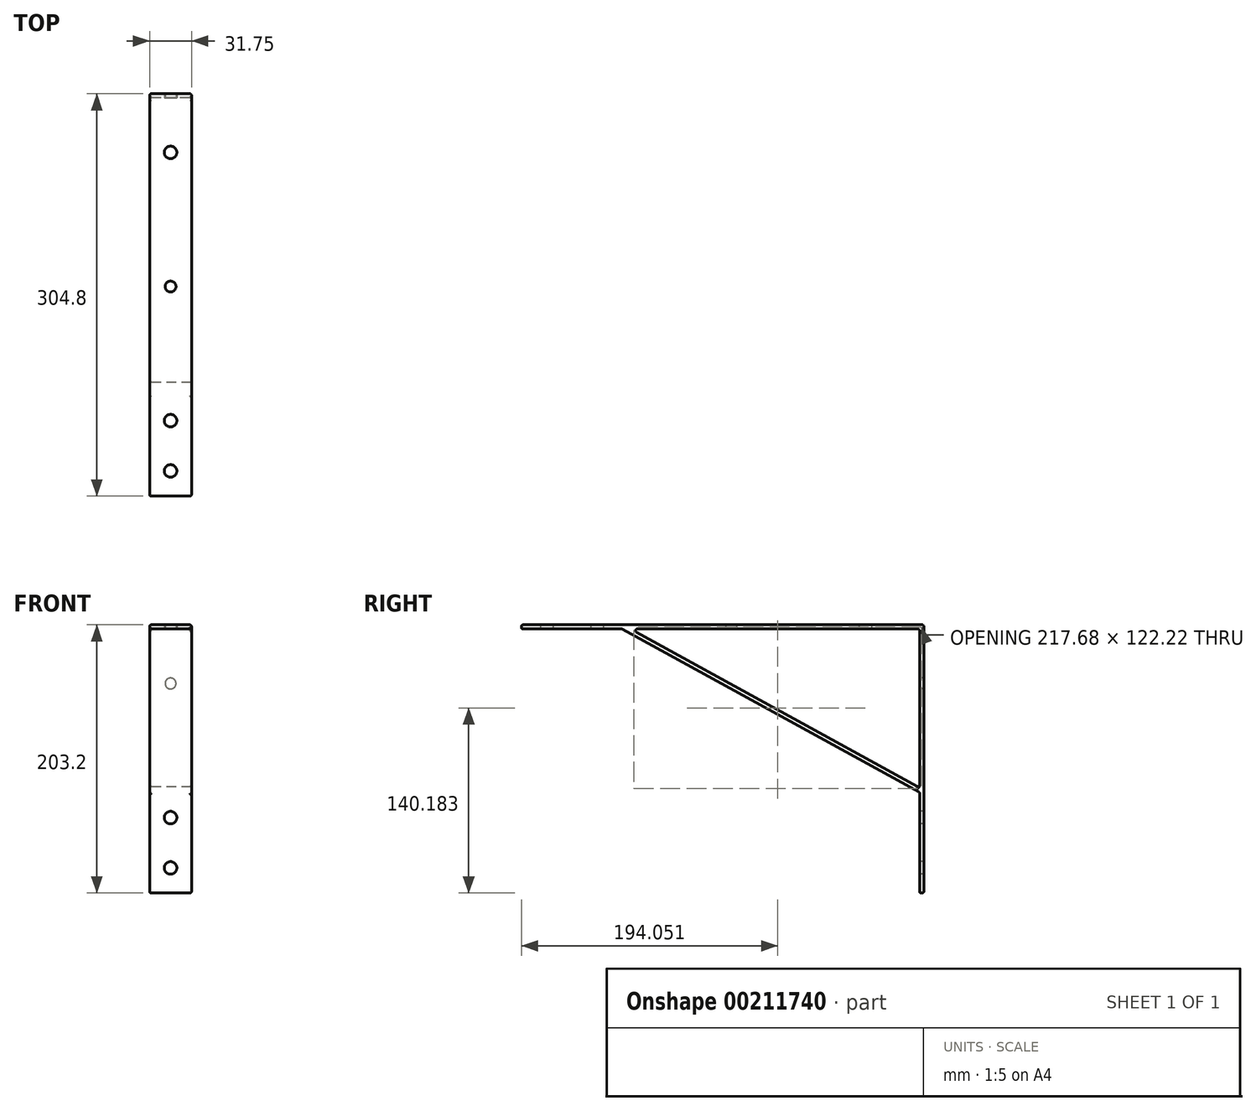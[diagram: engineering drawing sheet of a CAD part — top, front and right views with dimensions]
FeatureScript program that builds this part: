
annotation { "Feature Type Name" : "Feature", "Feature Type Description" : "" }
export const myFeature = defineFeature(function(context is Context, id is Id, definition is map)
    precondition{}
    {
        {
            var Q0;
            Q0=qCreatedBy(makeId("Right.planeOp"),FACE);
            var sketch = newSketch(context, id + "F0", { "sketchPlane" : qUnion([Q0])});
            skLineSegment(sketch, "E0", {"start": v(-304.8, 203.2) * mm, "end": v(0, 203.2) * mm});
            skLineSegment(sketch, "E1", {"start": v(0, 203.2) * mm, "end": v(0, 0) * mm});
            skLineSegment(sketch, "E2", {"start": v(0, 0) * mm, "end": v(-3.17, 0) * mm});
            skLineSegment(sketch, "E3", {"start": v(-3.17, 0) * mm, "end": v(-3.18, 76.2) * mm});
            skLineSegment(sketch, "E4", {"start": v(-3.18, 200.03) * mm, "end": v(-222, 200.02) * mm});
            skLineSegment(sketch, "E5", {"start": v(-304.8, 200.02) * mm, "end": v(-304.8, 203.2) * mm});
            skLineSegment(sketch, "E6", {"start": v(-222, 200.03) * mm, "end": v(-3.18, 79.82) * mm});
            skLineSegment(sketch, "E7", {"start": v(-3.18, 76.2) * mm, "end": v(-228.6, 200.02) * mm});
            skLineSegment(sketch, "E8.trimOffspring", {"start": v(-228.6, 200.02) * mm, "end": v(-304.8, 200.02) * mm});
            skLineSegment(sketch, "E9.trimOffspring", {"start": v(-3.18, 79.82) * mm, "end": v(-3.18, 200.03) * mm});
            skSolve(sketch);
        }
        {
            var Q0;
            Q0 = qSketchRegion(id + "F0", true);
            extrude(context, id + "F1", {"entities" : qUnion([Q0]), "depth" : 31.75 * mm});
        }
        {
            var Q0;
            Q0=makeQuery(id+"F1.opExtrude","CAP_EDGE",EDGE,{"disambiguationData":[OSD([sQuery(id+"F0.wireOp",EDGE,"E6")])],"isStart":false});
            var Q1;
            Q1=makeQuery(id+"F1.opExtrude","CAP_EDGE",EDGE,{"disambiguationData":[OSD([sQuery(id+"F0.wireOp",EDGE,"E7")])],"isStart":false});
            var Q2;
            Q2=makeQuery(id+"F1.opExtrude","CAP_EDGE",EDGE,{"disambiguationData":[OSD([sQuery(id+"F0.wireOp",EDGE,"E7")])],"isStart":true});
            var Q3;
            Q3=makeQuery(id+"F1.opExtrude","CAP_EDGE",EDGE,{"disambiguationData":[OSD([sQuery(id+"F0.wireOp",EDGE,"E6")])],"isStart":true});
            var Q4;
            Q4=makeQuery(id+"F1.opExtrude","SWEPT_EDGE",EDGE,{"disambiguationData":[OSD([sQuery(id+"F0.wireOp",EDGE,"E3"),sQuery(id+"F0.wireOp",EDGE,"E7")])]});
            var Q5;
            Q5=makeQuery(id+"F1.opExtrude","SWEPT_EDGE",EDGE,{"disambiguationData":[OSD([sQuery(id+"F0.wireOp",EDGE,"E7"),sQuery(id+"F0.wireOp",EDGE,"E8.trimOffspring")])]});
            fillet(context, id + "F2", {"entities" : qUnion([Q0, Q1, Q2, Q3, Q4, Q5]), "radius" : 1.27 * mm, "tangentPropagation" : true, "allowEdgeOverflow" : false});
        }
        {
            var Q0;
            Q0=makeQuery(id+"F1.opExtrude","SWEPT_EDGE",EDGE,{"disambiguationData":[OSD([sQuery(id+"F0.wireOp",EDGE,"E6"),sQuery(id+"F0.wireOp",EDGE,"E9.trimOffspring")])]});
            var Q1;
            Q1=makeQuery(id+"F1.opExtrude","SWEPT_EDGE",EDGE,{"disambiguationData":[OSD([sQuery(id+"F0.wireOp",EDGE,"E4"),sQuery(id+"F0.wireOp",EDGE,"E6")])]});
            var Q2;
            Q2=makeQuery(id+"F1.opExtrude","SWEPT_EDGE",EDGE,{"disambiguationData":[OSD([sQuery(id+"F0.wireOp",EDGE,"E4"),sQuery(id+"F0.wireOp",EDGE,"E9.trimOffspring")])]});
            var Q3;
            Q3=makeQuery(id+"F1.opExtrude","SWEPT_FACE",FACE,{"disambiguationData":[OSD([sQuery(id+"F0.wireOp",EDGE,"E0")])]});
            var Q4;
            Q4=makeQuery(id+"F1.opExtrude","SWEPT_FACE",FACE,{"disambiguationData":[OSD([sQuery(id+"F0.wireOp",EDGE,"E5")])]});
            var Q5;
            Q5=makeQuery(id+"F1.opExtrude","SWEPT_FACE",FACE,{"disambiguationData":[OSD([sQuery(id+"F0.wireOp",EDGE,"E4")])]});
            var Q6;
            Q6=makeQuery(id+"F1.opExtrude","SWEPT_FACE",FACE,{"disambiguationData":[OSD([sQuery(id+"F0.wireOp",EDGE,"E1")])]});
            var Q7;
            Q7=makeQuery(id+"F1.opExtrude","SWEPT_FACE",FACE,{"disambiguationData":[OSD([sQuery(id+"F0.wireOp",EDGE,"E2")])]});
            fillet(context, id + "F3", {"entities" : qUnion([Q0, Q1, Q2, Q3, Q4, Q5, Q6, Q7]), "radius" : 1.27 * mm, "tangentPropagation" : true, "allowEdgeOverflow" : false});
        }
        {
            var Q0;
            Q0=makeQuery(id+"F1.opExtrude","SWEPT_FACE",FACE,{"disambiguationData":[OSD([sQuery(id+"F0.wireOp",EDGE,"E8.trimOffspring")])]});
            var sketch = newSketch(context, id + "F4", { "sketchPlane" : qUnion([Q0])});
            skCircle(sketch, "E10", {"center": v(15.88, 285.75) * mm, "radius": 4.76 * mm});
            skCircle(sketch, "E11", {"center": v(15.88, 247.65) * mm, "radius": 4.76 * mm});
            skCircle(sketch, "E12", {"center": v(15.88, 146.05) * mm, "radius": 4.13 * mm});
            skCircle(sketch, "E13", {"center": v(15.88, 44.45) * mm, "radius": 4.76 * mm});
            skSolve(sketch);
        }
        {
            var Q0;
            Q0 = qSketchRegion(id + "F4", true);
            extrude(context, id + "F5", {"entities" : qUnion([Q0]), "operationType" : NewBodyOperationType.REMOVE, "endBound" : BoundingType.UP_TO_NEXT, "oppositeDirection" : true, "depth" : 25.4 * mm});
        }
        {
            var Q0;
            Q0=makeQuery(id+"F1.opExtrude","SWEPT_FACE",FACE,{"disambiguationData":[OSD([sQuery(id+"F0.wireOp",EDGE,"E3")])]});
            var sketch = newSketch(context, id + "F6", { "sketchPlane" : qUnion([Q0])});
            skCircle(sketch, "E14", {"center": v(15.87, 57.15) * mm, "radius": 4.76 * mm});
            skCircle(sketch, "E15", {"center": v(15.88, 19.05) * mm, "radius": 4.76 * mm});
            skCircle(sketch, "E16", {"center": v(15.88, 158.75) * mm, "radius": 4.13 * mm});
            skSolve(sketch);
        }
        {
            var Q0;
            Q0 = qSketchRegion(id + "F6", true);
            extrude(context, id + "F7", {"entities" : qUnion([Q0]), "operationType" : NewBodyOperationType.REMOVE, "endBound" : BoundingType.UP_TO_NEXT, "oppositeDirection" : true, "depth" : 25.4 * mm});
        }
    });
